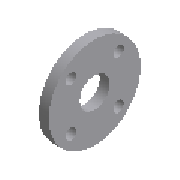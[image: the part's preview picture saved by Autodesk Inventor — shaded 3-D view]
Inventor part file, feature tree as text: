
AUTODESK INVENTOR PART (.ipt)
format: ipt  version: 2025 (Build 290162010, 162A)  size: 168,960 bytes
history: native  units: mm (DEFAULTED — no unit token found)
features: other x5, revolve x1, extrude x1, pattern_circular x1
ambient origin geometry x8: Origin, YZ Plane, XZ Plane, XY Plane, X Axis, Y Axis, Z Axis, Center Point
bodies: Solid1 (feature_tree)
feature tree (8):
  revolve  "Revolution1"  Angle=90.0deg
  extrude  "Extrusion1"  Depth=200.0mm
  pattern_circular  "Circular Pattern1"  Count=2  [1 undecoded]
  other  "Work Axis1"
  other  "Work Point1"
  other  "Work Axis2"
  other  "Work Point2"
  other  "Work Point3"
note: 1 required parameter value undecoded (feature->parameter linkage not recoverable at this tier; creation-order binding heuristic only, values carry confidence <= 0.55)
